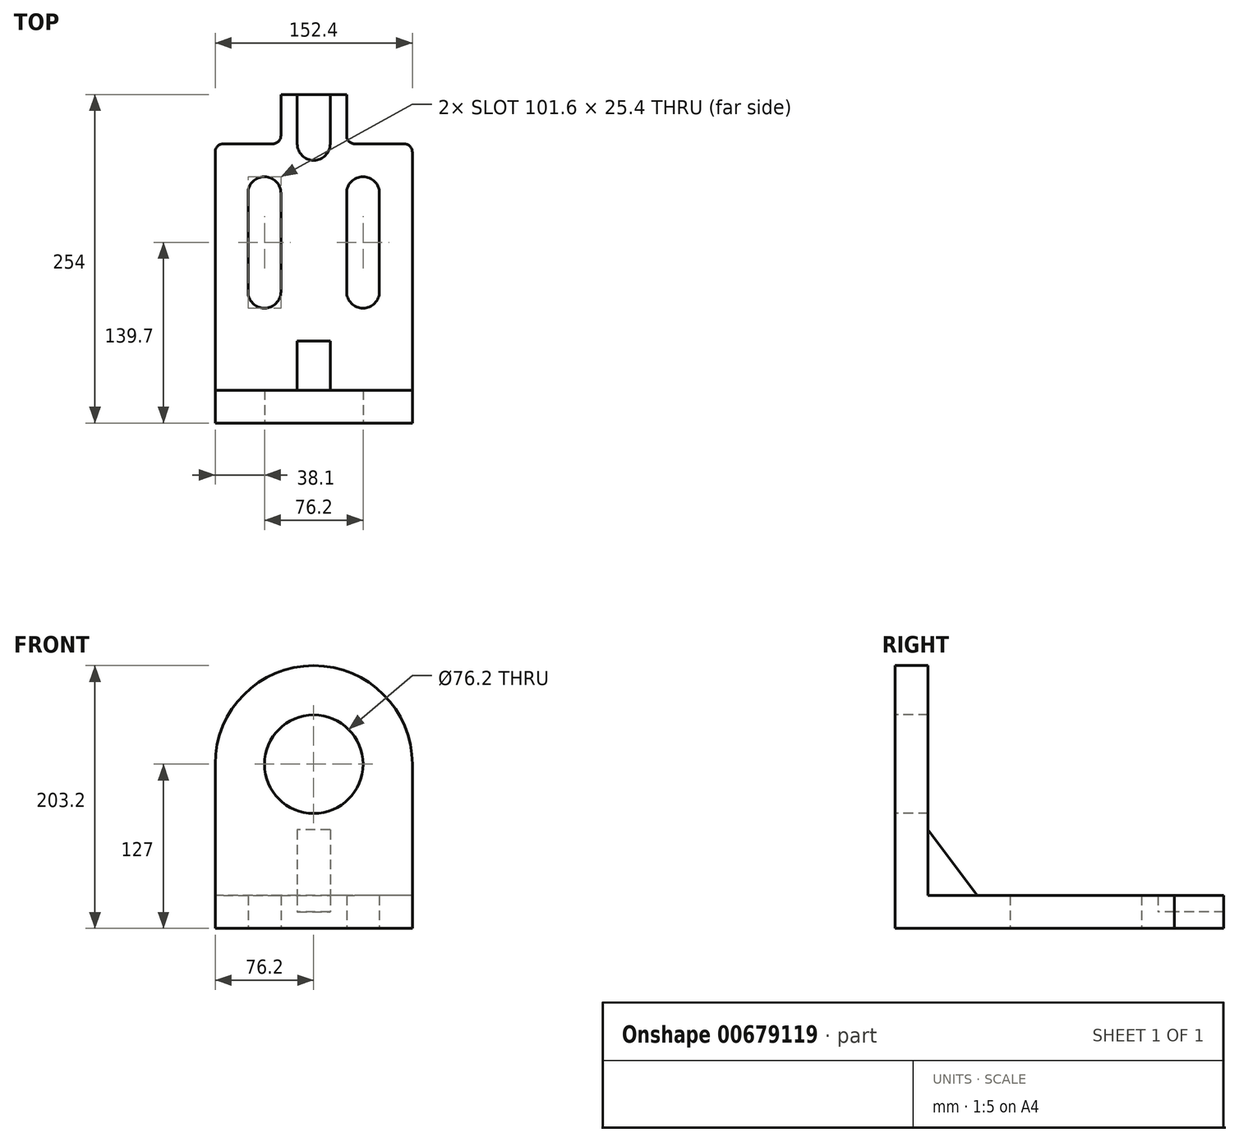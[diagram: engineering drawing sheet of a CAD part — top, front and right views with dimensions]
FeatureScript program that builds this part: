
annotation { "Feature Type Name" : "Feature", "Feature Type Description" : "" }
export const myFeature = defineFeature(function(context is Context, id is Id, definition is map)
    precondition{}
    {
        {
            var Q0;
            Q0=qCreatedBy(makeId("Top.planeOp"),FACE);
            var sketch = newSketch(context, id + "F0", { "sketchPlane" : qUnion([Q0])});
            skLineSegment(sketch, "E0", {"start": v(-76.2, 0) * mm, "end": v(-76.2, 209.55) * mm});
            skLineSegment(sketch, "E1", {"start": v(76.2, 209.55) * mm, "end": v(76.2, 0) * mm});
            skLineSegment(sketch, "E2", {"start": v(-69.85, 215.9) * mm, "end": v(-31.75, 215.9) * mm});
            skLineSegment(sketch, "E3", {"start": v(-25.4, 222.25) * mm, "end": v(-25.4, 254) * mm});
            skLineSegment(sketch, "E4", {"start": v(-25.4, 254) * mm, "end": v(-12.7, 254) * mm});
            skLineSegment(sketch, "E5", {"start": v(-12.7, 254) * mm, "end": v(-12.7, 215.9) * mm});
            skLineSegment(sketch, "E6", {"start": v(69.85, 215.9) * mm, "end": v(31.75, 215.9) * mm});
            skLineSegment(sketch, "E7", {"start": v(25.4, 222.25) * mm, "end": v(25.4, 254) * mm});
            skLineSegment(sketch, "E8", {"start": v(25.4, 254) * mm, "end": v(12.7, 254) * mm});
            skLineSegment(sketch, "E9", {"start": v(12.7, 254) * mm, "end": v(12.7, 215.9) * mm});
            skArc(sketch, "E10", {"start": v(-12.7, 215.9) * mm, "mid": v(0, 203.2) * mm, "end": v(12.7, 215.9) * mm});
            skPoint(sketch, "E11.visualSharp", {"position": v(25.4, 215.9) * mm});
            skArc(sketch, "E11.filletArc", {"start": v(25.4, 222.25) * mm, "mid": v(27.26, 217.76) * mm, "end": v(31.75, 215.9) * mm});
            skPoint(sketch, "E12.visualSharp", {"position": v(-25.4, 215.9) * mm});
            skArc(sketch, "E12.filletArc", {"start": v(-31.75, 215.9) * mm, "mid": v(-27.26, 217.76) * mm, "end": v(-25.4, 222.25) * mm});
            skPoint(sketch, "E13.visualSharp", {"position": v(-76.2, 215.9) * mm});
            skArc(sketch, "E13.filletArc", {"start": v(-69.85, 215.9) * mm, "mid": v(-74.34, 214.04) * mm, "end": v(-76.2, 209.55) * mm});
            skPoint(sketch, "E14.visualSharp", {"position": v(76.2, 215.9) * mm});
            skArc(sketch, "E14.filletArc", {"start": v(76.2, 209.55) * mm, "mid": v(74.34, 214.04) * mm, "end": v(69.85, 215.9) * mm});
            skLineSegment(sketch, "E15", {"start": v(-50.8, 177.8) * mm, "end": v(-50.8, 101.6) * mm});
            skLineSegment(sketch, "E16.0", {"start": v(-25.4, 177.8) * mm, "end": v(-25.4, 101.6) * mm});
            skLineSegment(sketch, "E17.0", {"start": v(25.4, 177.8) * mm, "end": v(25.4, 101.6) * mm});
            skLineSegment(sketch, "E18.0", {"start": v(50.8, 177.8) * mm, "end": v(50.8, 101.6) * mm});
            skArc(sketch, "E19", {"start": v(25.4, 177.8) * mm, "mid": v(38.1, 190.5) * mm, "end": v(50.8, 177.8) * mm});
            skArc(sketch, "E20", {"start": v(50.8, 101.6) * mm, "mid": v(38.1, 88.9) * mm, "end": v(25.4, 101.6) * mm});
            skArc(sketch, "E21", {"start": v(-25.4, 177.8) * mm, "mid": v(-38.1, 190.5) * mm, "end": v(-50.8, 177.8) * mm});
            skArc(sketch, "E22", {"start": v(-50.8, 101.6) * mm, "mid": v(-38.1, 88.9) * mm, "end": v(-25.4, 101.6) * mm});
            skLineSegment(sketch, "E23", {"start": v(-25.4, 222.25) * mm, "end": v(-12.7, 222.25) * mm});
            skLineSegment(sketch, "E24", {"start": v(25.4, 222.25) * mm, "end": v(12.7, 222.25) * mm});
            skLineSegment(sketch, "E25", {"start": v(-76.2, 0) * mm, "end": v(76.2, 0) * mm});
            skLineSegment(sketch, "E26", {"start": v(12.7, 254) * mm, "end": v(-12.7, 254) * mm});
            skSolve(sketch);
        }
        {
            var Q0;
            Q0=makeQuery(id+"F0.imprint","IMPRINT",FACE,{"disambiguationData":[TD([[makeQuery(id+"F0.imprint","IMPRINT",EDGE,{"derivedFrom":sQuery(id+"F0.wireOp",EDGE,"E2")}),-1.0]])]});
            var Q1;
            {var subQ5=sQuery(id+"F0.wireOp",EDGE,"ijPdRpkw-eoPW-TIoZ-kyqT-Oyow3i9Ip0rv");Q1=makeQuery(id+"F0.imprint","IMPRINT",FACE,{"disambiguationData":[TD([[makeQuery(id+"F0.imprint","IMPRINT",EDGE,{"derivedFrom":subQ5}),1.0]])]});}
            var Q2;
            {var subQ0=sQuery(id+"F0.wireOp",EDGE,"nf2URjwK-eU4i-GjXp-86dw-JJDDW09vTfEV");Q2=makeQuery(id+"F0.imprint","IMPRINT",FACE,{"disambiguationData":[TD([[makeQuery(id+"F0.imprint","IMPRINT",EDGE,{"derivedFrom":subQ0}),-1.0]])]});}
            extrude(context, id + "F1", {"entities" : qUnion([Q0, Q1, Q2]), "depth" : 25.4 * mm, "offsetDistance" : 25.4 * mm});
        }
        {
            var Q0;
            Q0=makeQuery(id+"F0.imprint","IMPRINT",FACE,{"disambiguationData":[TD([[makeQuery(id+"F0.imprint","IMPRINT",EDGE,{"derivedFrom":sQuery(id+"F0.wireOp",EDGE,"E3")}),-1.0]])]});
            var Q1;
            Q1=makeQuery(id+"F0.imprint","IMPRINT",FACE,{"disambiguationData":[TD([[makeQuery(id+"F0.imprint","IMPRINT",EDGE,{"derivedFrom":sQuery(id+"F0.wireOp",EDGE,"E7")}),1.0]])]});
            extrude(context, id + "F2", {"entities" : qUnion([Q0, Q1]), "operationType" : NewBodyOperationType.ADD, "depth" : 25.4 * mm, "offsetDistance" : 25.4 * mm});
        }
        {
            var Q0;
            Q0=qCreatedBy(makeId("Right.planeOp"),FACE);
            var sketch = newSketch(context, id + "F3", { "sketchPlane" : qUnion([Q0])});
            skLineSegment(sketch, "E27", {"start": v(0, 25.4) * mm, "end": v(0, 203.2) * mm});
            skLineSegment(sketch, "E28", {"start": v(0, 203.2) * mm, "end": v(25.4, 203.2) * mm});
            skLineSegment(sketch, "E29", {"start": v(25.4, 203.2) * mm, "end": v(25.4, 25.4) * mm});
            skLineSegment(sketch, "E30", {"start": v(0, 25.4) * mm, "end": v(63.5, 25.4) * mm});
            skLineSegment(sketch, "E31", {"start": v(25.4, 76.2) * mm, "end": v(63.5, 25.4) * mm});
            skSolve(sketch);
        }
        {
            var Q0;
            {var subQ3=sQuery(id+"F3.wireOp",EDGE,"E31");Q0=makeQuery(id+"F3.imprint","IMPRINT",FACE,{"disambiguationData":[TD([[makeQuery(id+"F3.imprint","IMPRINT",EDGE,{"derivedFrom":subQ3}),-1.0]])]});}
            extrude(context, id + "F4", {"entities" : qUnion([Q0]), "operationType" : NewBodyOperationType.ADD, "endBound" : BoundingType.SYMMETRIC, "depth" : 25.4 * mm, "offsetDistance" : 25.4 * mm});
        }
        {
            var Q0;
            Q0=qCreatedBy(makeId("Front.planeOp"),FACE);
            var sketch = newSketch(context, id + "F5", { "sketchPlane" : qUnion([Q0])});
            skSolve(sketch);
        }
        {
            var Q0;
            Q0=qCreatedBy(makeId("Front.planeOp"),FACE);
            var sketch = newSketch(context, id + "F6", { "sketchPlane" : qUnion([Q0])});
            skLineSegment(sketch, "E32", {"start": v(76.2, 25.4) * mm, "end": v(76.2, 127) * mm});
            skLineSegment(sketch, "E33", {"start": v(76.2, 25.4) * mm, "end": v(-76.2, 25.4) * mm});
            skLineSegment(sketch, "E34", {"start": v(-76.2, 25.4) * mm, "end": v(-76.2, 127) * mm});
            skLineSegment(sketch, "E35", {"start": v(0, 203.2) * mm, "end": v(0, 203.2) * mm});
            skPoint(sketch, "E36.visualSharp", {"position": v(76.2, 203.2) * mm});
            skArc(sketch, "E36.filletArc", {"start": v(76.2, 127) * mm, "mid": v(53.88, 180.88) * mm, "end": v(0, 203.2) * mm});
            skPoint(sketch, "E37.visualSharp", {"position": v(-76.2, 203.2) * mm});
            skArc(sketch, "E37.filletArc", {"start": v(0, 203.2) * mm, "mid": v(-53.88, 180.88) * mm, "end": v(-76.2, 127) * mm});
            skCircle(sketch, "E38", {"center": v(0, 127) * mm, "radius": 38.1 * mm});
            skSolve(sketch);
        }
        {
            var Q0;
            Q0 = qSketchRegion(id + "F5", true);
            var Q1;
            Q1=makeQuery(id+"F6.imprint","IMPRINT",FACE,{"disambiguationData":[TD([[makeQuery(id+"F6.imprint","IMPRINT",EDGE,{"derivedFrom":sQuery(id+"F6.wireOp",EDGE,"E32")}),1.0]])]});
            extrude(context, id + "F7", {"entities" : qUnion([Q0, Q1]), "operationType" : NewBodyOperationType.ADD, "oppositeDirection" : true, "depth" : 25.4 * mm, "offsetDistance" : 25.4 * mm});
        }
        {
            var Q0;
            {var subQ0=sQuery(id+"F0.wireOp",EDGE,"E10");Q0=makeQuery(id+"F0.imprint","IMPRINT",FACE,{"disambiguationData":[TD([[makeQuery(id+"F0.imprint","IMPRINT",EDGE,{"derivedFrom":subQ0}),1.0]])]});}
            extrude(context, id + "F8", {"entities" : qUnion([Q0]), "operationType" : NewBodyOperationType.ADD, "depth" : 12.7 * mm, "offsetDistance" : 25.4 * mm});
        }
    });
